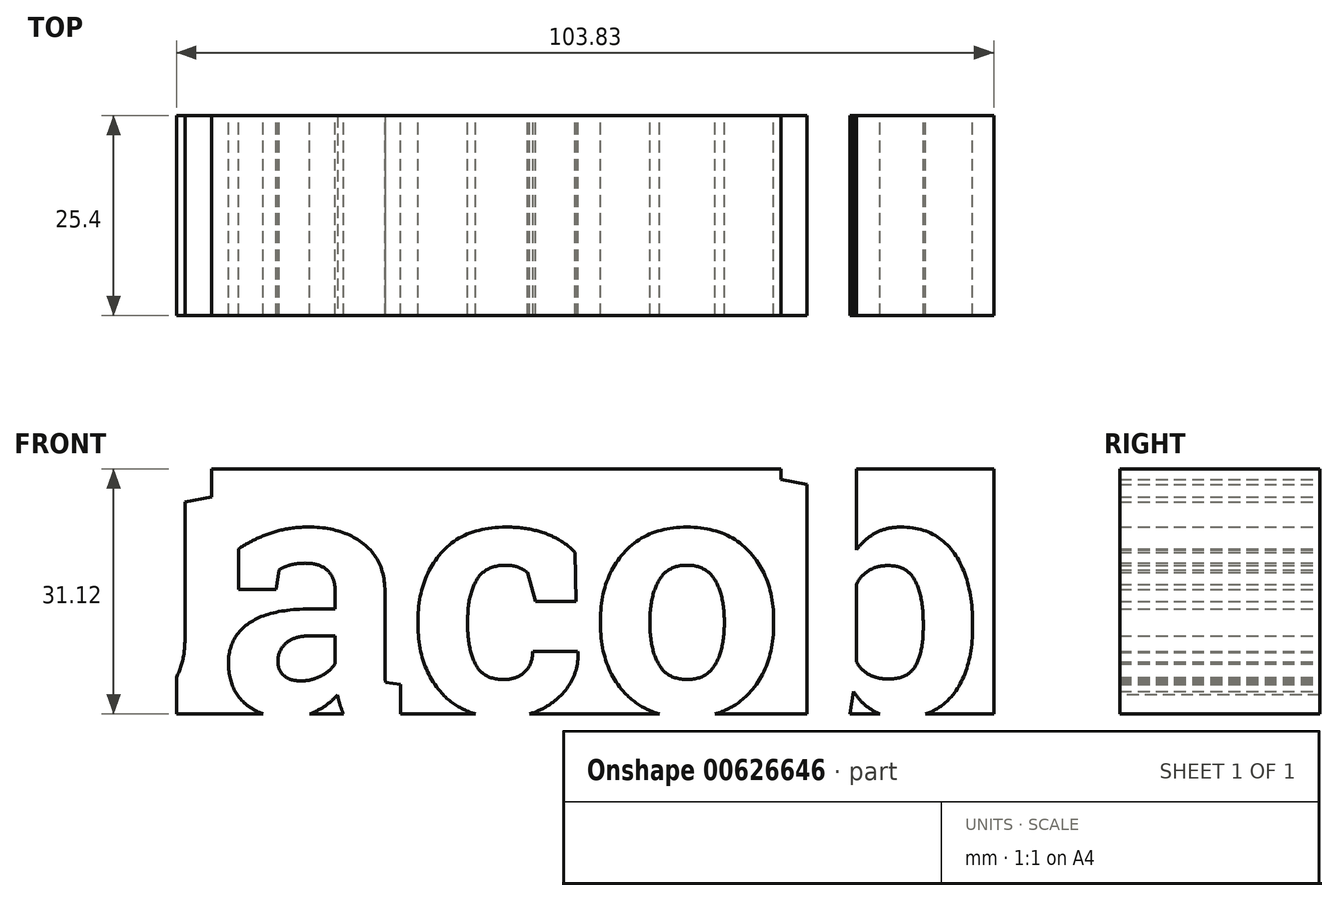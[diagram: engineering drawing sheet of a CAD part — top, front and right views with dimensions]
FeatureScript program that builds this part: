
annotation { "Feature Type Name" : "Feature", "Feature Type Description" : "" }
export const myFeature = defineFeature(function(context is Context, id is Id, definition is map)
    precondition{}
    {
        {
            var Q0;
            Q0=qCreatedBy(makeId("Front.planeOp"),FACE);
            var sketch = newSketch(context, id + "F0", { "sketchPlane" : qUnion([Q0])});
            skText(sketch, "E0", { "text": "Jacob ", "fontName": "RobotoSlab-Bold.ttf"});
            const initialGuessF0  = {"E0": [-0.1245, 0, 1, 0, 0.03177]};
            skSetInitialGuess(sketch, initialGuessF0);
            skSolve(sketch);
        }
        {
            var Q0;
            Q0=qCreatedBy(makeId("Front.planeOp"),FACE);
            var sketch = newSketch(context, id + "F1", { "sketchPlane" : qUnion([Q0])});
            skLineSegment(sketch, "E1.bottom", {"start": v(0, 0) * mm, "end": v(-103.83, 0) * mm});
            skLineSegment(sketch, "E1.top", {"start": v(0, 31.12) * mm, "end": v(-103.83, 31.12) * mm});
            skLineSegment(sketch, "E1.left", {"start": v(0, 0) * mm, "end": v(0, 31.12) * mm});
            skLineSegment(sketch, "E1.right", {"start": v(-103.83, 0) * mm, "end": v(-103.83, 31.12) * mm});
            skSolve(sketch);
        }
        {
            var Q0;
            Q0 = qSketchRegion(id + "F1", true);
            extrude(context, id + "F2", {"entities" : qUnion([Q0]), "depth" : 25.4 * mm, "offsetDistance" : 25.4 * mm});
        }
        {
            var Q0;
            Q0 = qSketchRegion(id + "F0", true);
            extrude(context, id + "F3", {"entities" : qUnion([Q0]), "operationType" : NewBodyOperationType.REMOVE, "depth" : 25.4 * mm, "offsetDistance" : 25.4 * mm});
        }
    });
